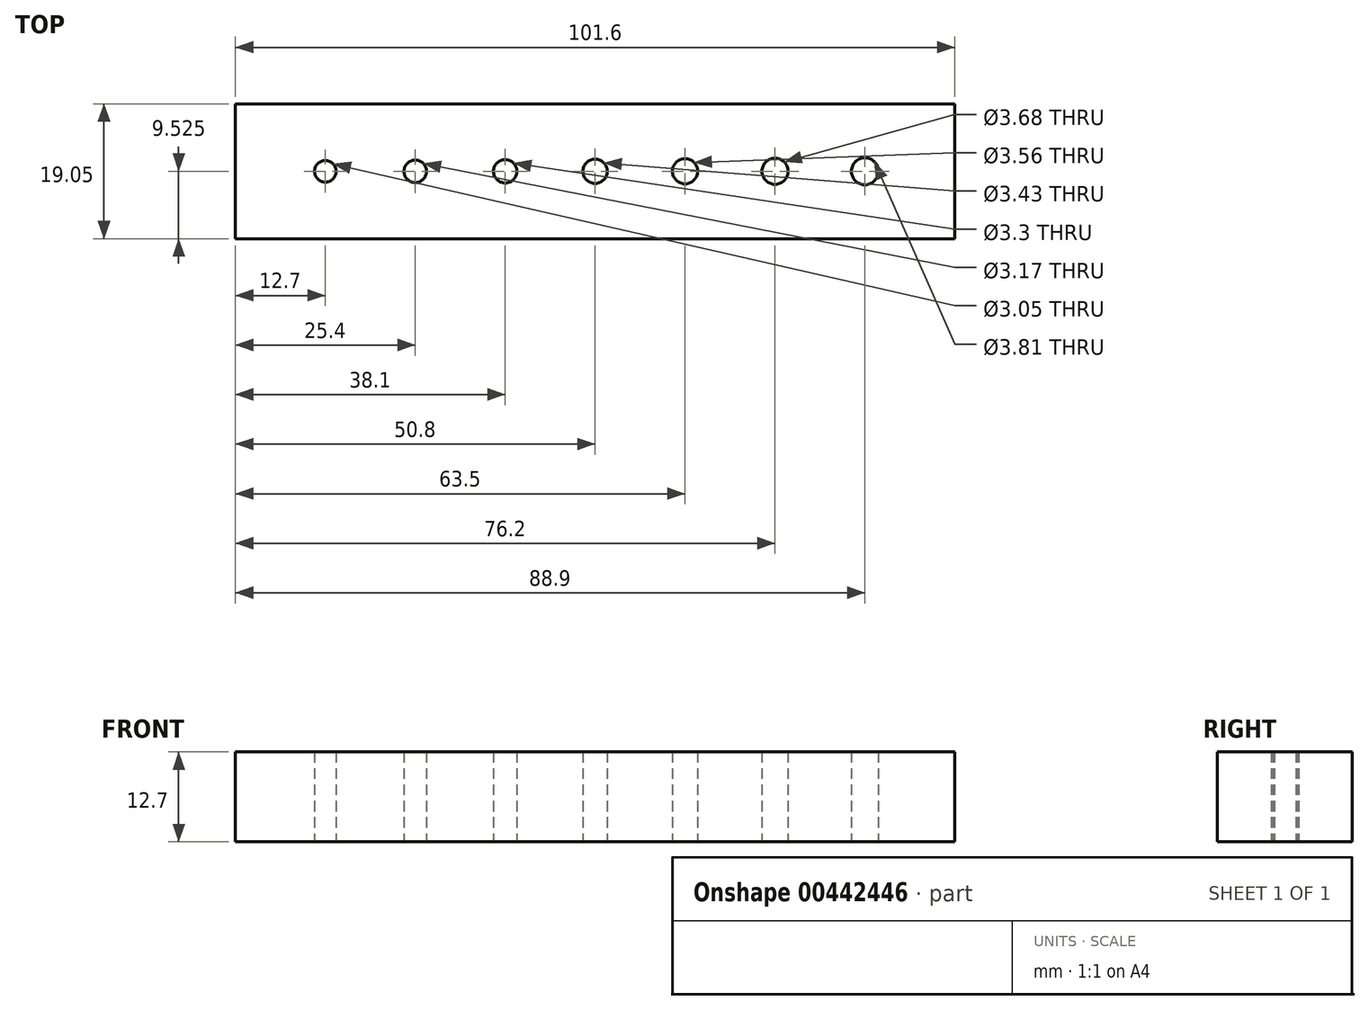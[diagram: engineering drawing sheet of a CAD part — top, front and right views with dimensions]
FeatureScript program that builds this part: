
annotation { "Feature Type Name" : "Feature", "Feature Type Description" : "" }
export const myFeature = defineFeature(function(context is Context, id is Id, definition is map)
    precondition{}
    {
        {
            var Q0;
            Q0=qCreatedBy(makeId("Top.planeOp"),FACE);
            var sketch = newSketch(context, id + "F0", { "sketchPlane" : qUnion([Q0])});
            skLineSegment(sketch, "E0.bottom", {"start": v(0, 0) * mm, "end": v(101.6, 0) * mm});
            skLineSegment(sketch, "E0.top", {"start": v(0, 19.05) * mm, "end": v(101.6, 19.05) * mm});
            skLineSegment(sketch, "E0.left", {"start": v(0, 0) * mm, "end": v(0, 19.05) * mm});
            skLineSegment(sketch, "E0.right", {"start": v(101.6, 0) * mm, "end": v(101.6, 19.05) * mm});
            skCircle(sketch, "E1", {"center": v(12.7, 9.52) * mm, "radius": 1.52 * mm});
            skCircle(sketch, "E2", {"center": v(25.4, 9.52) * mm, "radius": 1.59 * mm});
            skCircle(sketch, "E3", {"center": v(38.1, 9.52) * mm, "radius": 1.65 * mm});
            skCircle(sketch, "E4", {"center": v(50.8, 9.52) * mm, "radius": 1.71 * mm});
            skCircle(sketch, "E5", {"center": v(63.5, 9.52) * mm, "radius": 1.78 * mm});
            skCircle(sketch, "E6", {"center": v(76.2, 9.53) * mm, "radius": 1.84 * mm});
            skCircle(sketch, "E7", {"center": v(88.9, 9.53) * mm, "radius": 1.9 * mm});
            skSolve(sketch);
        }
        {
            var Q0;
            Q0=makeQuery(id+"F0.imprint","IMPRINT",FACE,{"disambiguationData":[TD([[makeQuery(id+"F0.imprint","IMPRINT",EDGE,{"derivedFrom":sQuery(id+"F0.wireOp",EDGE,"E0.bottom")}),1.0]])]});
            extrude(context, id + "F1", {"entities" : qUnion([Q0]), "depth" : 12.7 * mm});
        }
    });
